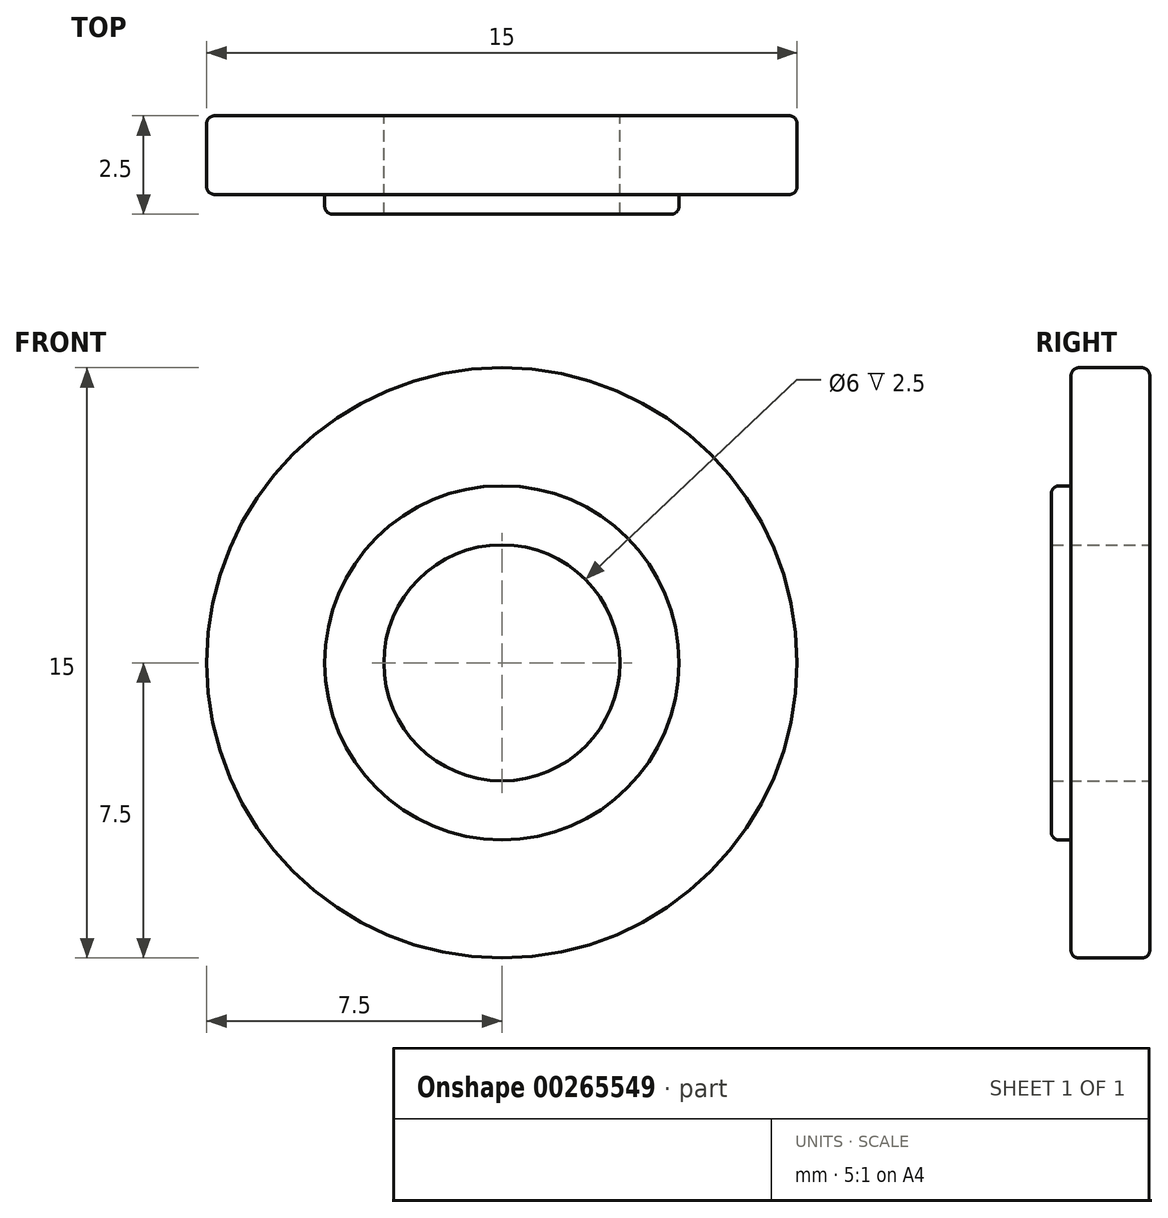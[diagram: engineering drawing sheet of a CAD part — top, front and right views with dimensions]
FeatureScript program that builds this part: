
annotation { "Feature Type Name" : "Feature", "Feature Type Description" : "" }
export const myFeature = defineFeature(function(context is Context, id is Id, definition is map)
    precondition{}
    {
        {
            var Q0;
            Q0=qCreatedBy(makeId("Front.planeOp"),FACE);
            var sketch = newSketch(context, id + "F0", { "sketchPlane" : qUnion([Q0])});
            skCircle(sketch, "E0", {"center": v(0, 0) * mm, "radius": 7.5 * mm});
            skCircle(sketch, "E1", {"center": v(0, 0) * mm, "radius": 3 * mm});
            skSolve(sketch);
        }
        {
            var Q0;
            Q0=makeQuery(id+"F0.imprint","IMPRINT",FACE,{"disambiguationData":[TD([[makeQuery(id+"F0.imprint","IMPRINT",EDGE,{"derivedFrom":sQuery(id+"F0.wireOp",EDGE,"E0")}),1.0]])]});
            extrude(context, id + "F1", {"entities" : qUnion([Q0]), "depth" : 2 * mm});
        }
        {
            var Q0;
            Q0=makeQuery(id+"F1.opExtrude","CAP_FACE",FACE,{"disambiguationData":[OSD([sQuery(id+"F0.wireOp",EDGE,"E0"),sQuery(id+"F0.wireOp",EDGE,"E1")])],"isStart":false});
            var sketch = newSketch(context, id + "F2", { "sketchPlane" : qUnion([Q0])});
            skCircle(sketch, "E2", {"center": v(0, 0) * mm, "radius": 4.5 * mm});
            skSolve(sketch);
        }
        {
            var Q0;
            Q0=makeQuery(id+"F2.imprint","IMPRINT",FACE,{"disambiguationData":[TD([[makeQuery(id+"F2.imprint","IMPRINT",EDGE,{"derivedFrom":sQuery(id+"F2.wireOp",EDGE,"E2")}),1.0]])]});
            extrude(context, id + "F3", {"entities" : qUnion([Q0]), "operationType" : NewBodyOperationType.ADD, "depth" : 0.5 * mm});
        }
        {
            var Q0;
            Q0=makeQuery(id+"F1.opExtrude","CAP_EDGE",EDGE,{"disambiguationData":[OSD([sQuery(id+"F0.wireOp",EDGE,"E0")])],"isStart":false});
            var Q1;
            Q1=makeQuery(id+"F1.opExtrude","CAP_EDGE",EDGE,{"disambiguationData":[OSD([sQuery(id+"F0.wireOp",EDGE,"E0")])],"isStart":true});
            var Q2;
            Q2=makeQuery(id+"F3.opExtrude","CAP_EDGE",EDGE,{"disambiguationData":[OSD([sQuery(id+"F2.wireOp",EDGE,"E2")])],"isStart":false});
            fillet(context, id + "F4", {"entities" : qUnion([Q0, Q1, Q2]), "radius" : 0.2 * mm, "tangentPropagation" : true, "allowEdgeOverflow" : false});
        }
    });
